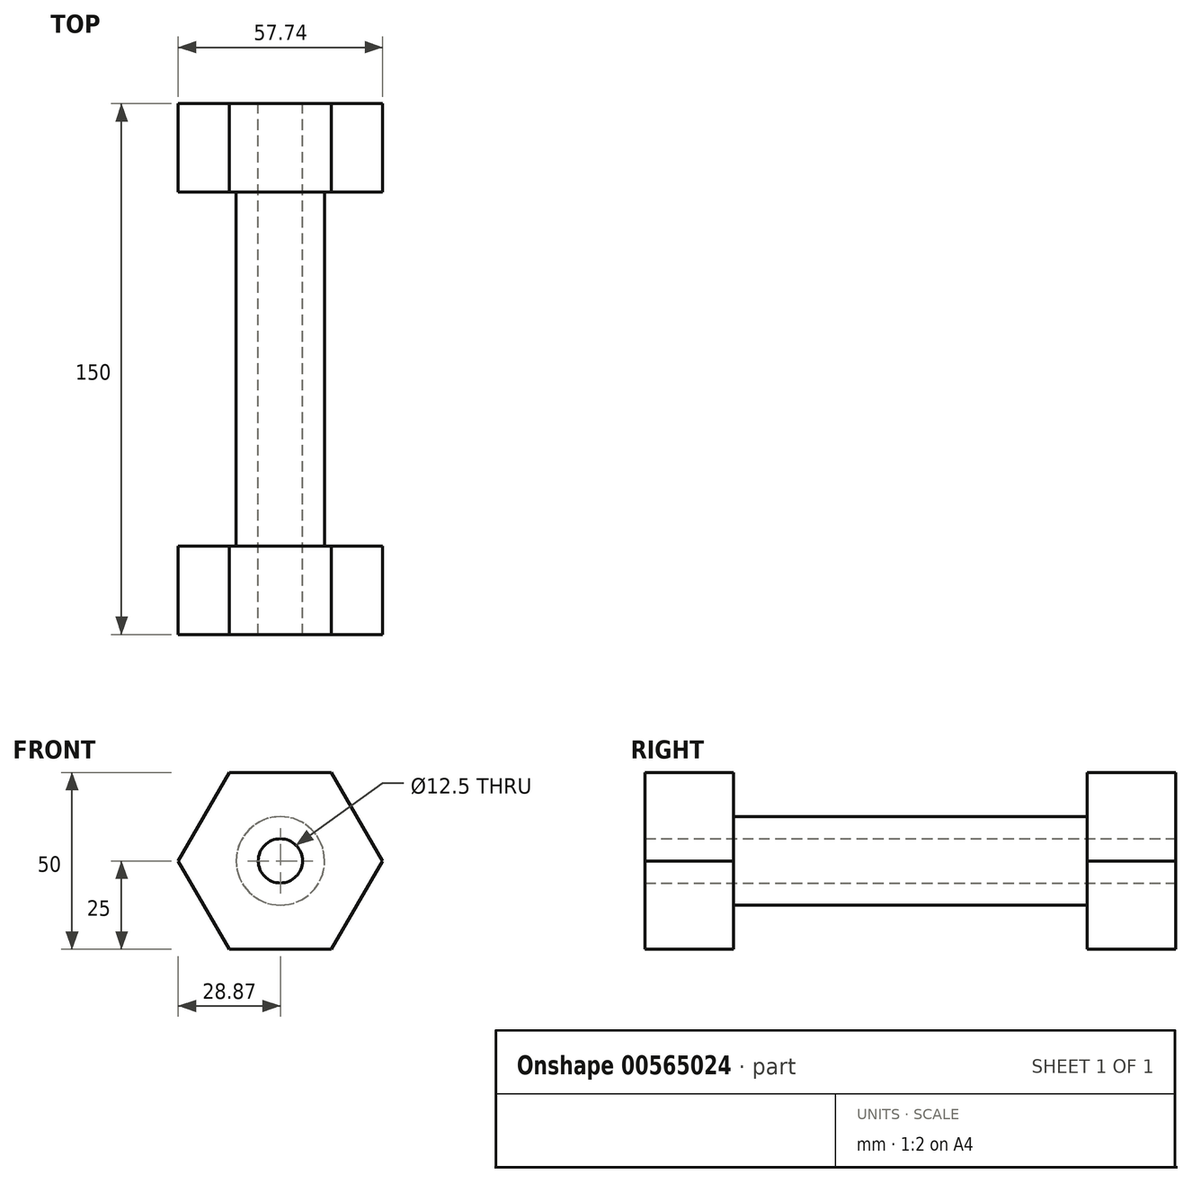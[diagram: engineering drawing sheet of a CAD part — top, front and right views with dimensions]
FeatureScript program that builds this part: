
annotation { "Feature Type Name" : "Feature", "Feature Type Description" : "" }
export const myFeature = defineFeature(function(context is Context, id is Id, definition is map)
    precondition{}
    {
        {
            var Q0;
            Q0=qCreatedBy(makeId("Front.planeOp"),FACE);
            var sketch = newSketch(context, id + "F0", { "sketchPlane" : qUnion([Q0])});
            skCircle(sketch, "E0.cCircle", {"center": v(0, 0) * mm, "radius": 25 * mm, "construction": true});
            skLineSegment(sketch, "E0.0", {"start": v(14.43, -25) * mm, "end": v(-14.43, -25) * mm});
            skLineSegment(sketch, "E0.1", {"start": v(-14.43, -25) * mm, "end": v(-28.87, 0) * mm});
            skLineSegment(sketch, "E0.2", {"start": v(-28.87, 0) * mm, "end": v(-14.43, 25) * mm});
            skLineSegment(sketch, "E0.3", {"start": v(-14.43, 25) * mm, "end": v(14.43, 25) * mm});
            skLineSegment(sketch, "E0.4", {"start": v(14.43, 25) * mm, "end": v(28.87, 0) * mm});
            skLineSegment(sketch, "E0.5", {"start": v(28.87, 0) * mm, "end": v(14.43, -25) * mm});
            skPoint(sketch, "E0.0.midPoint", {"position": v(0, -25) * mm});
            skCircle(sketch, "E1", {"center": v(0, 0) * mm, "radius": 12.5 * mm});
            skCircle(sketch, "E2", {"center": v(0, 0) * mm, "radius": 6.25 * mm});
            skSolve(sketch);
        }
        {
            var Q0;
            Q0=qSketchRegion(id+"F0",true);
            extrude(context, id + "F1", {"entities" : qUnion([Q0]), "depth" : 25 * mm, "offsetDistance" : 25 * mm});
        }
        {
            var Q0;
            Q0=makeQuery(id+"F1.opExtrude","CAP_FACE",FACE,{"disambiguationData":[OSD([sQuery(id+"F0.wireOp",EDGE,"E0.0"),sQuery(id+"F0.wireOp",EDGE,"E0.1"),sQuery(id+"F0.wireOp",EDGE,"E0.2"),sQuery(id+"F0.wireOp",EDGE,"E0.3"),sQuery(id+"F0.wireOp",EDGE,"E0.4"),sQuery(id+"F0.wireOp",EDGE,"E0.5"),sQuery(id+"F0.wireOp",EDGE,"E1")])],"isStart":false});
            var sketch = newSketch(context, id + "F2", { "sketchPlane" : qUnion([Q0])});
            skCircle(sketch, "E3.0", {"center": v(0, 0) * mm, "radius": 12.5 * mm});
            skCircle(sketch, "E4.0", {"center": v(0, 0) * mm, "radius": 6.25 * mm});
            skSolve(sketch);
        }
        {
            var Q0;
            Q0=qSketchRegion(id+"F2",true);
            extrude(context, id + "F3", {"entities" : qUnion([Q0]), "depth" : 50 * mm, "offsetDistance" : 25 * mm});
        }
        {
            var Q0;
            Q0=makeQuery(id+"F0.imprint","IMPRINT",FACE,{"disambiguationData":[TD([[makeQuery(id+"F0.imprint","IMPRINT",EDGE,{"derivedFrom":sQuery(id+"F0.wireOp",EDGE,"E0.0")}),-1.0]])]});
            var sketch = newSketch(context, id + "F4", { "sketchPlane" : qUnion([Q0])});
            skCircle(sketch, "E5.0", {"center": v(0, 0) * mm, "radius": 12.5 * mm});
            skCircle(sketch, "E6.0", {"center": v(0, 0) * mm, "radius": 6.25 * mm});
            skSolve(sketch);
        }
        {
            var Q0;
            Q0=qSketchRegion(id+"F4",true);
            extrude(context, id + "F5", {"entities" : qUnion([Q0]), "depth" : 25 * mm, "offsetDistance" : 25 * mm});
        }
        {
            var Q0;
            Q0=makeQuery(id+"F3.opExtrude","SWEPT_BODY",BODY,{"disambiguationData":[OSD([sQuery(id+"F2.wireOp",EDGE,"E3.0"),sQuery(id+"F2.wireOp",EDGE,"E4.0")])]});
            var Q1;
            Q1=makeQuery(id+"F1.opExtrude","SWEPT_BODY",BODY,{"disambiguationData":[OSD([sQuery(id+"F0.wireOp",EDGE,"E0.0"),sQuery(id+"F0.wireOp",EDGE,"E0.1"),sQuery(id+"F0.wireOp",EDGE,"E0.2"),sQuery(id+"F0.wireOp",EDGE,"E0.3"),sQuery(id+"F0.wireOp",EDGE,"E0.4"),sQuery(id+"F0.wireOp",EDGE,"E0.5"),sQuery(id+"F0.wireOp",EDGE,"E1")])]});
            var Q2;
            Q2=makeQuery(id+"F5.opExtrude","SWEPT_BODY",BODY,{"disambiguationData":[OSD([sQuery(id+"F4.wireOp",EDGE,"E5.0"),sQuery(id+"F4.wireOp",EDGE,"E6.0")])]});
            var Q3;
            Q3=makeQuery(id+"F3.opExtrude","CAP_FACE",FACE,{"disambiguationData":[OSD([sQuery(id+"F2.wireOp",EDGE,"E3.0"),sQuery(id+"F2.wireOp",EDGE,"E4.0")])],"isStart":false});
            mirror(context, id + "F6", {"operationType" : NewBodyOperationType.ADD, "entities" : qUnion([Q0, Q1, Q2]), "mirrorPlane" : qUnion([Q3])});
        }
    });
